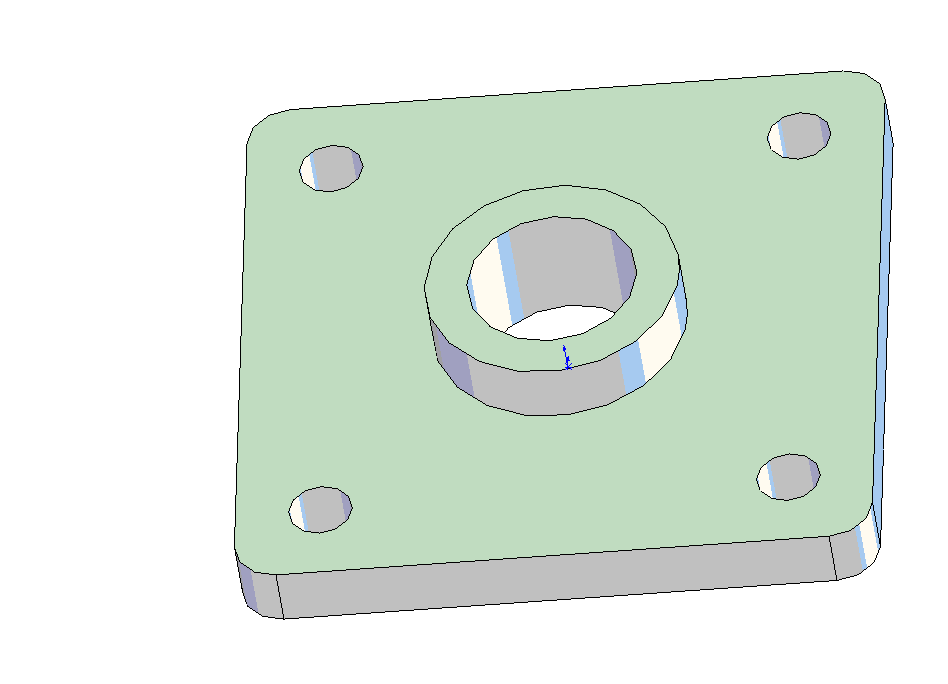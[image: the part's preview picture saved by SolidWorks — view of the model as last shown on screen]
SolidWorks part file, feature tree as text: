
SOLIDWORKS PART (.sldprt)
format: sldprt  version: not decoded by parser v0  size: 133,632 bytes
history: native  units: mm
features: sketch x4, extrude x2, cut_extrude x2, material x1, fillet x1 (+13 scaffold rows collapsed)
feature tree (23):
  scaffold x13  (default folders/planes/origin — collapsed)
  material  "Material <not specified>"
  sketch  "Sketch1"  dims[D1=95.25mm]
  extrude  "Extrude1"  Depth=9.525mm
  sketch  "Sketch2"  dims[D1=38.1mm]
  extrude  "Extrude2"  Depth=9.525mm
  sketch  "Sketch3"  dims[D1=25.4mm]
  cut_extrude  "Cut-Extrude1"  [1 undecoded]
  fillet  "Fillet1"  Radius=6.35mm
  sketch  "Sketch4"  dims[c1.D2=9.525mm c1.D1=69.85mm c2.D2=~6.186169mm]
  cut_extrude  "Cut-Extrude2"  [1 undecoded]
decode coverage: 7 of 9 modeling features carry decoded parameters
note: ~ marks probable driven/reference dimensions
note: 2 parameter values undecoded
note: suppression state not decoded; provenance and decode notes live in map.json
